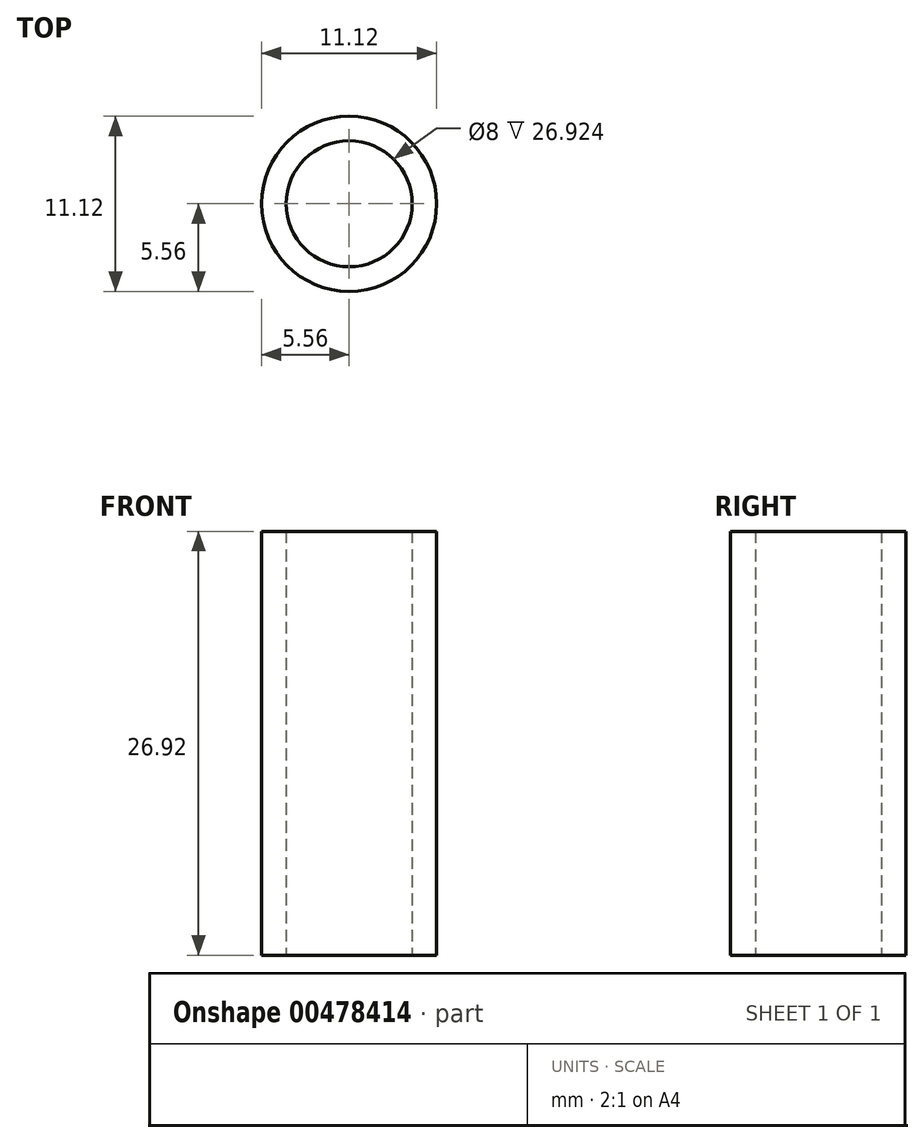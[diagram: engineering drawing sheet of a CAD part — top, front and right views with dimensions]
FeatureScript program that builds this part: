
annotation { "Feature Type Name" : "Feature", "Feature Type Description" : "" }
export const myFeature = defineFeature(function(context is Context, id is Id, definition is map)
    precondition{}
    {
        {
            var Q0;
            Q0=qCreatedBy(makeId("Top.planeOp"),FACE);
            var sketch = newSketch(context, id + "F0", { "sketchPlane" : qUnion([Q0])});
            skCircle(sketch, "E0", {"center": v(0, 0) * mm, "radius": 4 * mm});
            skCircle(sketch, "E1", {"center": v(0, 0) * mm, "radius": 5.56 * mm});
            skSolve(sketch);
        }
        {
            var Q0;
            Q0 = qSketchRegion(id + "F0", true);
            extrude(context, id + "F1", {"entities" : qUnion([Q0]), "depth" : 26.92 * mm});
        }
    });
